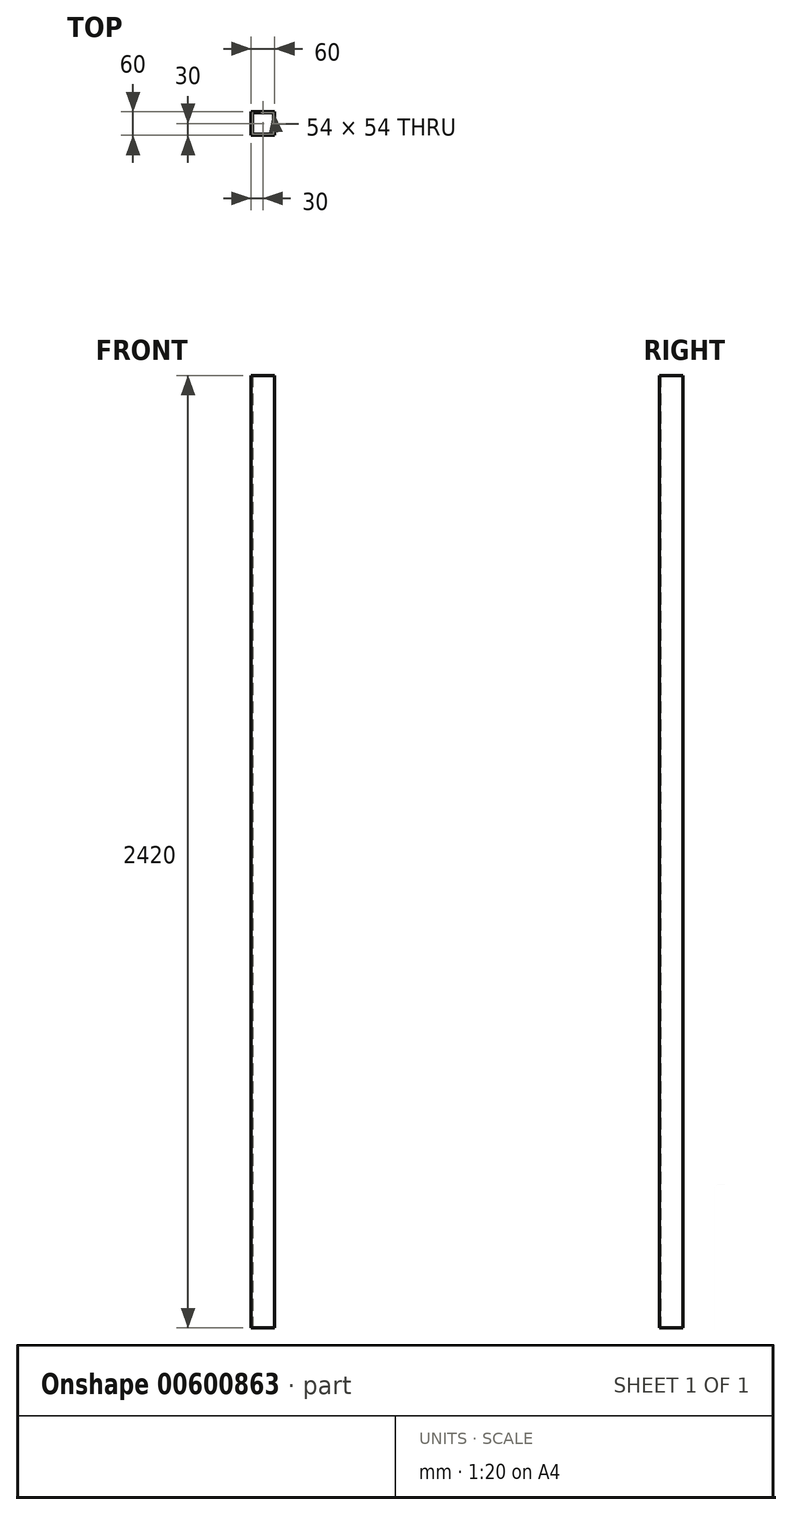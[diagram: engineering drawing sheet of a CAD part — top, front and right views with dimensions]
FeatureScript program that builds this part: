
annotation { "Feature Type Name" : "Feature", "Feature Type Description" : "" }
export const myFeature = defineFeature(function(context is Context, id is Id, definition is map)
    precondition{}
    {
        {
            var Q0;
            Q0=qCreatedBy(makeId("Top.planeOp"),FACE);
            var sketch = newSketch(context, id + "F0", { "sketchPlane" : qUnion([Q0])});
            skLineSegment(sketch, "E0.bottom", {"start": v(0, 0) * mm, "end": v(60, 0) * mm});
            skLineSegment(sketch, "E0.top", {"start": v(0, 60) * mm, "end": v(60, 60) * mm});
            skLineSegment(sketch, "E0.left", {"start": v(0, 0) * mm, "end": v(0, 60) * mm});
            skLineSegment(sketch, "E0.right", {"start": v(60, 0) * mm, "end": v(60, 60) * mm});
            skLineSegment(sketch, "E1.bottom", {"start": v(3, 57) * mm, "end": v(57, 57) * mm});
            skLineSegment(sketch, "E1.top", {"start": v(3, 3) * mm, "end": v(57, 3) * mm});
            skLineSegment(sketch, "E1.left", {"start": v(3, 57) * mm, "end": v(3, 3) * mm});
            skLineSegment(sketch, "E1.right", {"start": v(57, 57) * mm, "end": v(57, 3) * mm});
            skSolve(sketch);
        }
        {
            var Q0;
            Q0=makeQuery(id+"F0.imprint","IMPRINT",FACE,{"disambiguationData":[TD([[makeQuery(id+"F0.imprint","IMPRINT",EDGE,{"derivedFrom":sQuery(id+"F0.wireOp",EDGE,"E0.bottom")}),1.0]])]});
            extrude(context, id + "F1", {"entities" : qUnion([Q0]), "depth" : 2420 * mm, "offsetDistance" : 25 * mm});
        }
    });
